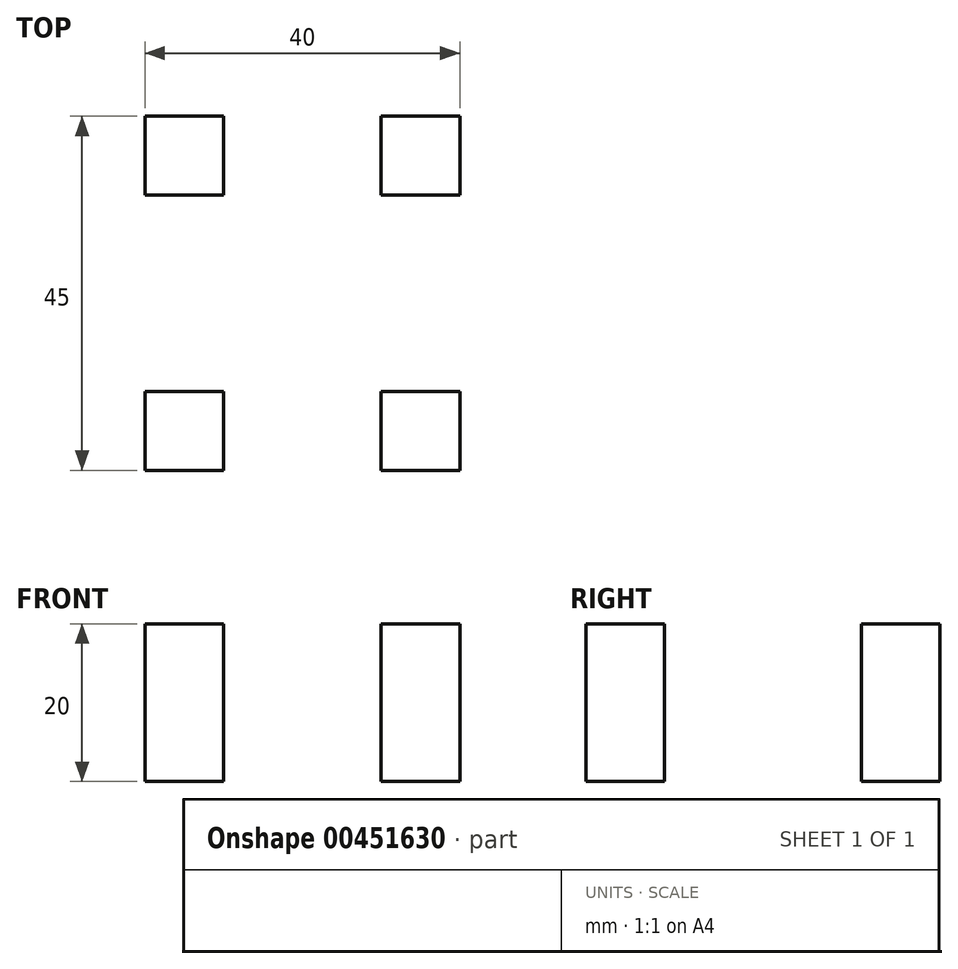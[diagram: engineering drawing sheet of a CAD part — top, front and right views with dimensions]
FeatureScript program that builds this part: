
annotation { "Feature Type Name" : "Feature", "Feature Type Description" : "" }
export const myFeature = defineFeature(function(context is Context, id is Id, definition is map)
    precondition{}
    {
        {
            var Q0;
            Q0=qCreatedBy(makeId("Top.planeOp"),FACE);
            var sketch = newSketch(context, id + "F0", { "sketchPlane" : qUnion([Q0])});
            skLineSegment(sketch, "E0.bottom", {"start": v(-5, 5) * mm, "end": v(5, 5) * mm});
            skLineSegment(sketch, "E0.top", {"start": v(-5, -5) * mm, "end": v(5, -5) * mm});
            skLineSegment(sketch, "E0.left", {"start": v(-5, 5) * mm, "end": v(-5, -5) * mm});
            skLineSegment(sketch, "E0.right", {"start": v(5, 5) * mm, "end": v(5, -5) * mm});
            skPoint(sketch, "E0.middle", {"position": v(0, 0) * mm});
            skLineSegment(sketch, "E1.0.1.0", {"start": v(-5, 40) * mm, "end": v(5, 40) * mm});
            skLineSegment(sketch, "E1.0.1.1", {"start": v(-5, 40) * mm, "end": v(-5, 30) * mm});
            skLineSegment(sketch, "E1.0.1.2", {"start": v(-5, 30) * mm, "end": v(5, 30) * mm});
            skLineSegment(sketch, "E1.0.1.3", {"start": v(5, 40) * mm, "end": v(5, 30) * mm});
            skLineSegment(sketch, "E1.1.0.0", {"start": v(25, 5) * mm, "end": v(35, 5) * mm});
            skLineSegment(sketch, "E1.1.0.1", {"start": v(25, 5) * mm, "end": v(25, -5) * mm});
            skLineSegment(sketch, "E1.1.0.2", {"start": v(25, -5) * mm, "end": v(35, -5) * mm});
            skLineSegment(sketch, "E1.1.0.3", {"start": v(35, 5) * mm, "end": v(35, -5) * mm});
            skLineSegment(sketch, "E1.1.1.0", {"start": v(25, 40) * mm, "end": v(35, 40) * mm});
            skLineSegment(sketch, "E1.1.1.1", {"start": v(25, 40) * mm, "end": v(25, 30) * mm});
            skLineSegment(sketch, "E1.1.1.2", {"start": v(25, 30) * mm, "end": v(35, 30) * mm});
            skLineSegment(sketch, "E1.1.1.3", {"start": v(35, 40) * mm, "end": v(35, 30) * mm});
            skLineSegment(sketch, "E1.direction1", {"start": v(-5, 5) * mm, "end": v(25, 5) * mm, "construction": true});
            skLineSegment(sketch, "E1.direction2", {"start": v(-5, 5) * mm, "end": v(-5, 40) * mm, "construction": true});
            skSolve(sketch);
        }
        {
            var Q0;
            Q0=makeQuery(id+"F0.imprint","IMPRINT",FACE,{"disambiguationData":[TD([[makeQuery(id+"F0.imprint","IMPRINT",EDGE,{"derivedFrom":sQuery(id+"F0.wireOp",EDGE,"E0.bottom")}),-1.0]])]});
            var Q1;
            Q1=makeQuery(id+"F0.imprint","IMPRINT",FACE,{"disambiguationData":[TD([[makeQuery(id+"F0.imprint","IMPRINT",EDGE,{"derivedFrom":sQuery(id+"F0.wireOp",EDGE,"E1.1.0.0")}),-1.0]])]});
            var Q2;
            Q2=makeQuery(id+"F0.imprint","IMPRINT",FACE,{"disambiguationData":[TD([[makeQuery(id+"F0.imprint","IMPRINT",EDGE,{"derivedFrom":sQuery(id+"F0.wireOp",EDGE,"E1.1.1.0")}),-1.0]])]});
            var Q3;
            Q3=makeQuery(id+"F0.imprint","IMPRINT",FACE,{"disambiguationData":[TD([[makeQuery(id+"F0.imprint","IMPRINT",EDGE,{"derivedFrom":sQuery(id+"F0.wireOp",EDGE,"E1.0.1.0")}),-1.0]])]});
            extrude(context, id + "F1", {"entities" : qUnion([Q0, Q1, Q2, Q3]), "depth" : 20 * mm});
        }
    });
